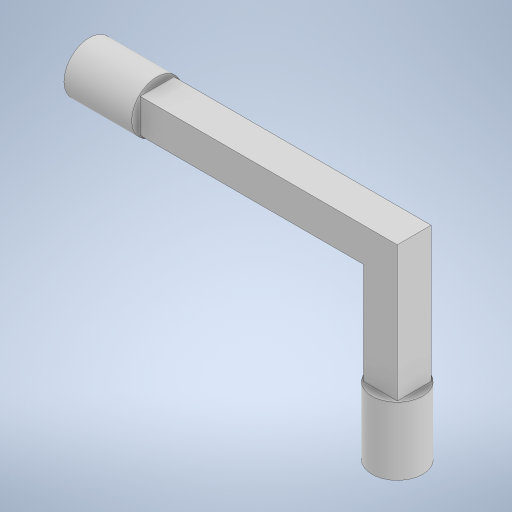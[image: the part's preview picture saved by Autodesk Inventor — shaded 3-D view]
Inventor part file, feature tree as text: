
AUTODESK INVENTOR PART (.ipt)
format: ipt  version: 2024.3 (Build 283343000, 343)  size: 249,856 bytes
history: native  units: mm
features: extrude x3, sketch x3, other x1
ambient origin geometry x8: Origin, YZ Plane, XZ Plane, XY Plane, X Axis, Y Axis, Z Axis, Center Point
bodies: Body1 (feature_tree)
feature tree (7):
  other  "ソリッド1"
  extrude  "押し出し1"  Depth=96.0mm
  extrude  "押し出し2"  Depth=60.0mm
  extrude  "押し出し3"  Depth=10.0mm
  sketch  "スケッチ1"
  sketch  "スケッチ2"
  sketch  "スケッチ3"
